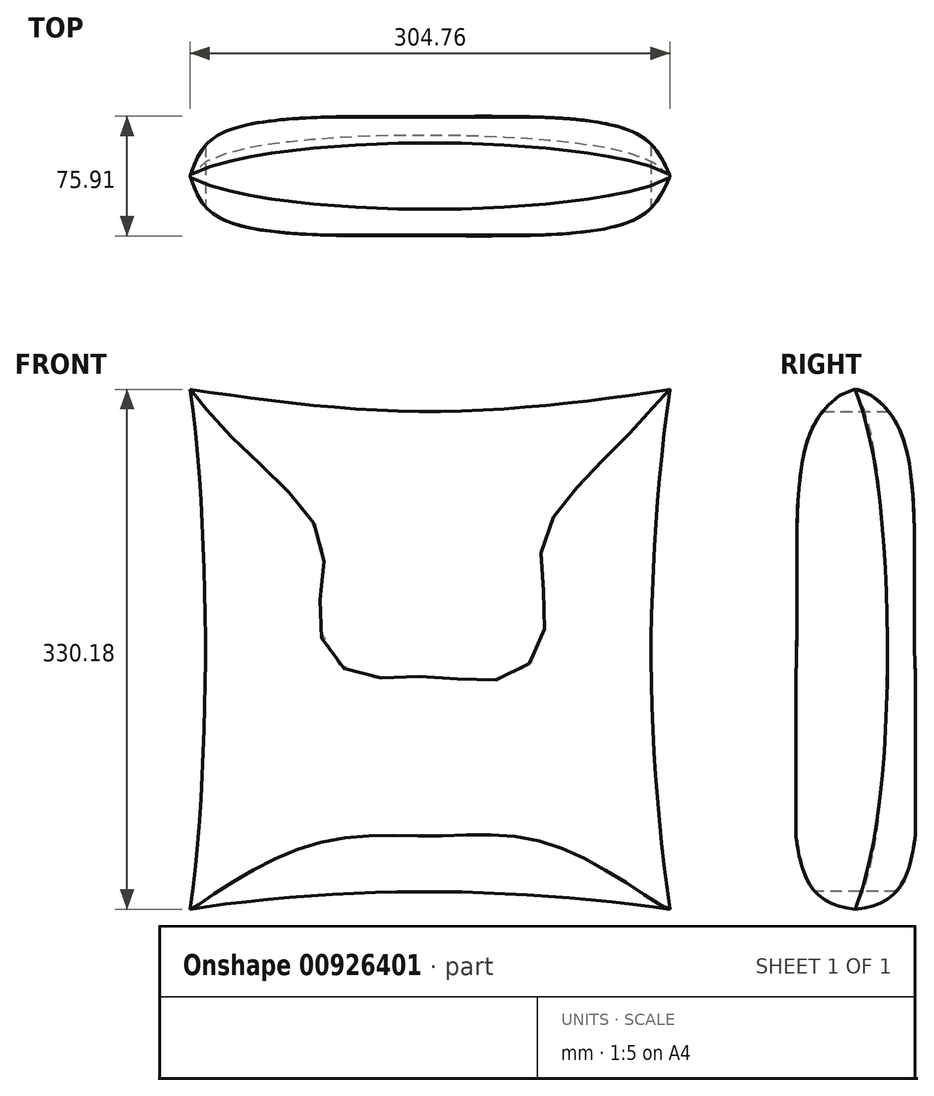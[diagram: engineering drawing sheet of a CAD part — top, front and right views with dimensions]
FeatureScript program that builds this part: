
annotation { "Feature Type Name" : "Feature", "Feature Type Description" : "" }
export const myFeature = defineFeature(function(context is Context, id is Id, definition is map)
    precondition{}
    {
        {
            var Q0;
            Q0=qCreatedBy(makeId("Front.planeOp"),FACE);
            var sketch = newSketch(context, id + "F0", { "sketchPlane" : qUnion([Q0])});
            skLineSegment(sketch, "E0.bottom", {"start": v(298.9, -45.42) * mm, "end": v(-5.9, -45.42) * mm, "construction": true});
            skLineSegment(sketch, "E0.top", {"start": v(298.9, 284.78) * mm, "end": v(-5.9, 284.78) * mm, "construction": true});
            skLineSegment(sketch, "E0.left", {"start": v(298.9, -45.42) * mm, "end": v(298.9, 284.78) * mm, "construction": true});
            skLineSegment(sketch, "E0.right", {"start": v(-5.9, -45.42) * mm, "end": v(-5.9, 284.78) * mm, "construction": true});
            skFitSpline(sketch, "E1", {"points": [v(-5.9, 284.78) * mm, v(140.67, 270.77) * mm, v(298.9, 284.78) * mm], "startDerivative": vector(151.16, -21.43) * mm, "endDerivative": vector(182.77, 27.89) * mm});
            skFitSpline(sketch, "E2", {"points": [v(298.9, 284.78) * mm, v(286.86, 113.45) * mm, v(298.9, -45.42) * mm], "startDerivative": vector(-25.35, -158.3) * mm, "endDerivative": vector(24.9, -171.78) * mm});
            skFitSpline(sketch, "E3", {"points": [v(298.9, -45.42) * mm, v(141.95, -34.25) * mm, v(-5.9, -45.42) * mm], "startDerivative": vector(-183.7, 26.6) * mm, "endDerivative": vector(-166.86, -27.74) * mm});
            skFitSpline(sketch, "E4", {"points": [v(-5.9, 284.78) * mm, v(3.87, 116.28) * mm, v(-5.9, -45.42) * mm], "startDerivative": vector(28.65, -164.47) * mm, "endDerivative": vector(-28.21, -172.62) * mm});
            skSolve(sketch);
        }
        {
            var Q0;
            Q0 = qSketchRegion(id + "F0", true);
            extrude(context, id + "F1", {"entities" : qUnion([Q0]), "depth" : 76.2 * mm, "offsetDistance" : 25.4 * mm});
        }
        {
            var Q0;
            Q0=qCreatedBy(makeId("Right.planeOp"),FACE);
            var sketch = newSketch(context, id + "F2", { "sketchPlane" : qUnion([Q0])});
            skLineSegment(sketch, "E5", {"start": v(-38.16, -45.4) * mm, "end": v(-38.16, 284.92) * mm, "construction": true});
            skLineSegment(sketch, "E6", {"start": v(-38.16, -24.76) * mm, "end": v(-38.16, -45.4) * mm, "construction": true});
            skLineSegment(sketch, "E7", {"start": v(-38.16, -24.76) * mm, "end": v(-76.53, -24.76) * mm, "construction": true});
            skLineSegment(sketch, "E8", {"start": v(-38.67, 119.66) * mm, "end": v(-38.67, 99.02) * mm, "construction": true});
            skLineSegment(sketch, "E9", {"start": v(-38.67, 99.02) * mm, "end": v(-76.28, 99.02) * mm, "construction": true});
            skLineSegment(sketch, "E10", {"start": v(-75.63, 119.76) * mm, "end": v(-38.16, 119.76) * mm, "construction": true});
            skFitSpline(sketch, "E11", {"points": [v(-38.16, 284.92) * mm, v(-65.43, 260.85) * mm, v(-75.63, 119.76) * mm, v(-65.72, -32.2) * mm, v(-38.16, -45.4) * mm], "startDerivative": vector(-156.47, -28.73) * mm, "endDerivative": vector(132.92, -13.37) * mm});
            skFitSpline(sketch, "E12.MirrorCS", {"points": [v(-38.16, 284.92) * mm, v(-10.9, 260.85) * mm, v(-0.7, 119.76) * mm, v(-10.6, -32.2) * mm, v(-38.16, -45.4) * mm], "startDerivative": vector(156.47, -28.73) * mm, "endDerivative": vector(-132.92, -13.37) * mm});
            skLineSegment(sketch, "E13", {"start": v(-38.16, -45.4) * mm, "end": v(-38.16, -45.4) * mm});
            skCircle(sketch, "E14", {"center": v(-38.16, 119.76) * mm, "radius": 445.3 * mm});
            skSolve(sketch);
        }
        {
            var Q0;
            Q0 = qSketchRegion(id + "F2", true);
            extrude(context, id + "F3", {"entities" : qUnion([Q0]), "operationType" : NewBodyOperationType.REMOVE, "oppositeDirection" : true, "depth" : 25.4 * mm, "offsetDistance" : 25.4 * mm});
        }
        {
            var Q0;
            Q0 = qSketchRegion(id + "F2", true);
            extrude(context, id + "F4", {"entities" : qUnion([Q0]), "operationType" : NewBodyOperationType.REMOVE, "depth" : 2540 * mm, "offsetDistance" : 25.4 * mm});
        }
        {
            var Q0;
            Q0=qCreatedBy(makeId("Top.planeOp"),FACE);
            var sketch = newSketch(context, id + "F5", { "sketchPlane" : qUnion([Q0])});
            skLineSegment(sketch, "E15", {"start": v(-5.9, -38.16) * mm, "end": v(298.85, -38.16) * mm, "construction": true});
            skLineSegment(sketch, "E16", {"start": v(-5.9, -38.16) * mm, "end": v(32.18, -38.16) * mm, "construction": true});
            skLineSegment(sketch, "E17", {"start": v(146.47, -38.16) * mm, "end": v(146.47, -76.03) * mm, "construction": true});
            skLineSegment(sketch, "E18.MirrorCS", {"start": v(298.85, -38.16) * mm, "end": v(260.76, -38.16) * mm, "construction": true});
            skLineSegment(sketch, "E19", {"start": v(32.18, -38.16) * mm, "end": v(32.18, -76.13) * mm, "construction": true});
            skLineSegment(sketch, "E20.MirrorCS", {"start": v(260.76, -38.16) * mm, "end": v(260.76, -76.13) * mm, "construction": true});
            skFitSpline(sketch, "E21", {"points": [v(-5.9, -38.16) * mm, v(12.26, -64.39) * mm, v(146.47, -76.03) * mm, v(277.1, -65.43) * mm, v(298.85, -38.16) * mm], "startDerivative": vector(63.18, -184.39) * mm, "endDerivative": vector(77.6, 193.7) * mm});
            skFitSpline(sketch, "E22.MirrorCS", {"points": [v(-5.9, -38.16) * mm, v(12.26, -11.94) * mm, v(146.47, -0.3) * mm, v(277.1, -10.9) * mm, v(298.85, -38.16) * mm], "startDerivative": vector(63.18, 184.39) * mm, "endDerivative": vector(77.6, -193.7) * mm});
            skCircle(sketch, "E23", {"center": v(146.47, -38.16) * mm, "radius": 187.74 * mm});
            skSolve(sketch);
        }
        {
            var Q0;
            Q0 = qSketchRegion(id + "F5", true);
            extrude(context, id + "F6", {"entities" : qUnion([Q0]), "operationType" : NewBodyOperationType.REMOVE, "oppositeDirection" : true, "depth" : 304.8 * mm, "offsetDistance" : 25.4 * mm});
        }
        {
            var Q0;
            Q0 = qSketchRegion(id + "F5", true);
            extrude(context, id + "F7", {"entities" : qUnion([Q0]), "operationType" : NewBodyOperationType.REMOVE, "depth" : 508 * mm, "offsetDistance" : 25.4 * mm});
        }
    });
